# Revit family: QF_BOURGEAT_Self_meuble_cuve_froid_statique_baie_libre_6GN
name_source: partatom
category: Equipement spécialisé
revit_build: Autodesk Revit 2015 (Build: 20140606_1530(x64)
units: mm (PartAtom-declared; Revit-internal decimal feet)

## types (24) — shared parameters
Charge max = 200.00 kg
Classe_climatique = 3
Fabricant = BOURGEAT
Fréquence = 50 Hz
Indice de protection = 21
Longueur hors tout = 2184 mm  [stored 7.16535 ft]
Nature isolant = polyurethane
Niveau Sonore = 60dBa
Phase = 2
Pieds_centre = Non
Profondeur hors tout = 820 mm  [stored 2.69029 ft]
Puissance frigorifique = 396W
Spécification du Fabricant = meuble cuve froid statique OASIS
Tension = 230 V
Type Fluide Frigorigène = R404a
URL catalogue = http://www.bourgeat.fr
porte_reserve = Non

## per-type parameters (varying)
| type | Hauteur hors tout | Intensité nominale | Modèle | Pieds | Poids net à vide | Puissance électrique  | Roues | etageres | presentoir | profondeur_cuve |
| baie _libre_cuve30 | 900 mm  [stored 2.95276 ft] | 4 A | 853026 | Oui | 300.00 kg | 1000 W | Non | Non | Non | 30 mm  [stored 0.0984252 ft] |
| baie _libre_cuve90 | 900 mm  [stored 2.95276 ft] | 4 A | 853096 | Oui | 300.00 kg | 1000 W | Non | Non | Non | 90 mm  [stored 0.295276 ft] |
| baie _libre_cuve30_presentoir_lampe_fluorecente | 1330 mm  [stored 4.36352 ft] | 5 A | 853026 + 853316 | Oui | 330.00 kg | 1048 W | Non | Non | Oui | 30 mm  [stored 0.0984252 ft] |
| baie _libre_cuve30_presentoir_lampe_LED | 1330 mm  [stored 4.36352 ft] | 5 A | 853026 + 853326 | Oui | 330.00 kg | 1048 W | Non | Non | Oui | 30 mm  [stored 0.0984252 ft] |
| baie _libre_cuve90_presentoir_lampe_LED | 1330 mm  [stored 4.36352 ft] | 5 A | 853096 + 853326 | Oui | 330.00 kg | 1048 W | Non | Non | Oui | 90 mm  [stored 0.295276 ft] |
| baie _libre_cuve90_presentoir_lampe_fluorecente | 1330 mm  [stored 4.36352 ft] | 5 A | 853096 + 853316 | Oui | 330.00 kg | 1048 W | Non | Non | Oui | 90 mm  [stored 0.295276 ft] |
| baie _libre_cuve30_roues | 900 mm  [stored 2.95276 ft] | 4 A | 853026 + 854950 | Non | 300.00 kg | 1000 W | Oui | Non | Non | 30 mm  [stored 0.0984252 ft] |
| baie _libre_cuve90_roues | 900 mm  [stored 2.95276 ft] | 4 A | 853096 + 854950 | Non | 300.00 kg | 1000 W | Oui | Non | Non | 90 mm  [stored 0.295276 ft] |
| baie _libre_cuve30_etageres | 900 mm  [stored 2.95276 ft] | 4 A | 853026 + 854916 | Oui | 300.00 kg | 1000 W | Non | Oui | Non | 30 mm  [stored 0.0984252 ft] |
| baie _libre_cuve90_etageres | 900 mm  [stored 2.95276 ft] | 4 A | 853096 + 854916 | Oui | 300.00 kg | 1000 W | Non | Oui | Non | 90 mm  [stored 0.295276 ft] |
| baie _libre_cuve30_presentoir_lampe_fluorecente_etageres | 1330 mm  [stored 4.36352 ft] | 5 A | 853026 + 853316 + 854916 | Oui | 330.00 kg | 1048 W | Non | Oui | Oui | 30 mm  [stored 0.0984252 ft] |
| baie _libre_cuve30_presentoir_lampe_LED_etageres | 1330 mm  [stored 4.36352 ft] | 5 A | 853026 + 853326 + 854916 | Oui | 330.00 kg | 1048 W | Non | Oui | Oui | 30 mm  [stored 0.0984252 ft] |
| baie _libre_cuve90_presentoir_lampe_fluorecente_etageres | 1330 mm  [stored 4.36352 ft] | 5 A | 853096 + 853316 + 854916 | Oui | 330.00 kg | 1048 W | Non | Oui | Oui | 90 mm  [stored 0.295276 ft] |
| baie _libre_cuve90_presentoir_lampe_LED_etageres | 1330 mm  [stored 4.36352 ft] | 5 A | 853096 + 853326 + 854916 | Oui | 330.00 kg | 1048 W | Non | Oui | Oui | 90 mm  [stored 0.295276 ft] |
| baie _libre_cuve30_presentoir_lampe_fluorecente_roues | 1330 mm  [stored 4.36352 ft] | 5 A | 853026 + 853316 + 854950 | Oui | 330.00 kg | 1048 W | Non | Non | Oui | 30 mm  [stored 0.0984252 ft] |
| baie _libre_cuve30_presentoir_lampe_LED_roues | 1330 mm  [stored 4.36352 ft] | 5 A | 853026 + 853326 + 854950 | Oui | 330.00 kg | 1048 W | Oui | Non | Oui | 30 mm  [stored 0.0984252 ft] |
| baie _libre_cuve90_presentoir_lampe_fluorecente_roues | 1330 mm  [stored 4.36352 ft] | 5 A | 853096 + 853316 + 854950 | Oui | 330.00 kg | 1048 W | Oui | Non | Oui | 90 mm  [stored 0.295276 ft] |
| baie _libre_cuve90_presentoir_lampe_LED_roues | 1330 mm  [stored 4.36352 ft] | 5 A | 853096 + 853326 + 854950 | Oui | 330.00 kg | 1048 W | Oui | Non | Oui | 90 mm  [stored 0.295276 ft] |
| baie _libre_cuve30_etageres_roues | 900 mm  [stored 2.95276 ft] | 4 A | 853026 + 854916 + 854950 | Oui | 300.00 kg | 1000 W | Oui | Oui | Non | 30 mm  [stored 0.0984252 ft] |
| baie _libre_cuve90_etageres_roues | 900 mm  [stored 2.95276 ft] | 4 A | 853096 + 854916 + 854950 | Oui | 300.00 kg | 1000 W | Oui | Oui | Non | 90 mm  [stored 0.295276 ft] |
| baie _libre_cuve30_presentoir_lampe_fluorecente_etageres_roues | 1330 mm  [stored 4.36352 ft] | 5 A | 853026 + 853316 + 854916 + 854950 | Oui | 330.00 kg | 1048 W | Oui | Oui | Oui | 30 mm  [stored 0.0984252 ft] |
| baie _libre_cuve30_presentoir_lampe_LED_etageres_roues | 1330 mm  [stored 4.36352 ft] | 5 A | 853026 + 853326 + 854916 + 854950 | Oui | 330.00 kg | 1048 W | Oui | Oui | Oui | 30 mm  [stored 0.0984252 ft] |
| baie _libre_cuve90_presentoir_lampe_fluorecente_etageres_roues | 1330 mm  [stored 4.36352 ft] | 5 A | 853096 + 853316 + 854916 + 854950 | Oui | 330.00 kg | 1048 W | Oui | Oui | Oui | 90 mm  [stored 0.295276 ft] |
| baie _libre_cuve90_presentoir_lampe_LED_etageres_roues | 1330 mm  [stored 4.36352 ft] | 5 A | 853096 + 853326 + 854916 + 854950 | Oui | 330.00 kg | 1048 W | Oui | Oui | Oui | 90 mm  [stored 0.295276 ft] |

note: [stored X ft] marks values corroborated as IEEE doubles in the binary element streams (Revit-internal decimal feet)

## geometry (parser evidence)
native form markers: Blend x4
no freeform markers — native parametric forms only
